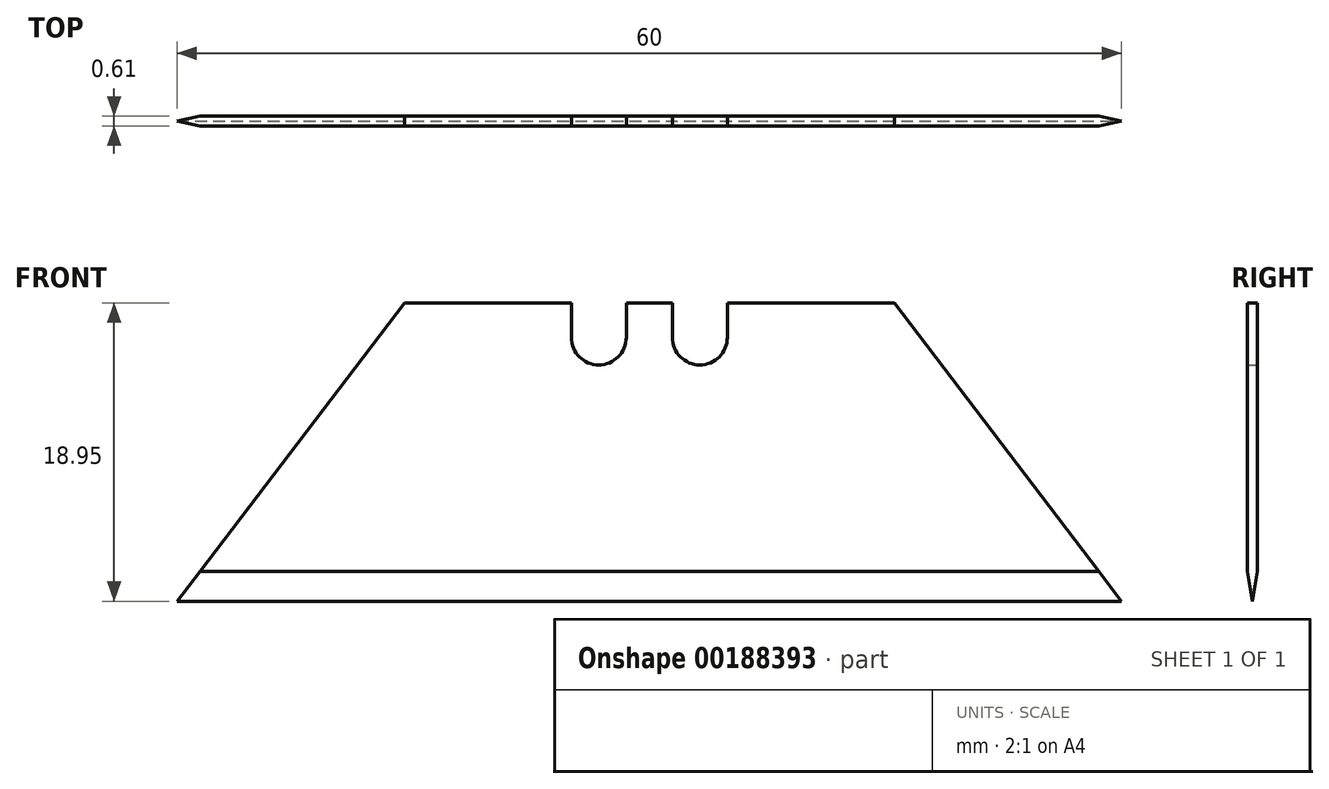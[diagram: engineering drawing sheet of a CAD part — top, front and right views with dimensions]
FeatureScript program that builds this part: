
annotation { "Feature Type Name" : "Feature", "Feature Type Description" : "" }
export const myFeature = defineFeature(function(context is Context, id is Id, definition is map)
    precondition{}
    {
        {
            var Q0;
            Q0=qCreatedBy(makeId("Front.planeOp"),FACE);
            var sketch = newSketch(context, id + "F0", { "sketchPlane" : qUnion([Q0])});
            skLineSegment(sketch, "E0", {"start": v(0, -18.95) * mm, "end": v(-14.44, 0) * mm});
            skLineSegment(sketch, "E1", {"start": v(-14.44, 0) * mm, "end": v(-25.04, 0) * mm});
            skLineSegment(sketch, "E2", {"start": v(-45.56, 0) * mm, "end": v(-60, -18.95) * mm});
            skLineSegment(sketch, "E3", {"start": v(-60, -18.95) * mm, "end": v(0, -18.95) * mm});
            skLineSegment(sketch, "E4", {"start": v(-30, 0) * mm, "end": v(-30, -18.95) * mm, "construction": true});
            skLineSegment(sketch, "E5", {"start": v(-28.54, 0) * mm, "end": v(-28.54, -2.2) * mm});
            skArc(sketch, "E6", {"start": v(-28.54, -2.2) * mm, "mid": v(-26.79, -3.94) * mm, "end": v(-25.04, -2.2) * mm});
            skLineSegment(sketch, "E7", {"start": v(-25.04, -2.2) * mm, "end": v(-25.04, 0) * mm});
            skLineSegment(sketch, "E8.MirrorCS", {"start": v(-31.46, 0) * mm, "end": v(-31.46, -2.2) * mm});
            skArc(sketch, "E9.MirrorCS", {"start": v(-31.46, -2.2) * mm, "mid": v(-33.21, -3.94) * mm, "end": v(-34.96, -2.2) * mm});
            skLineSegment(sketch, "E10.MirrorCS", {"start": v(-34.96, -2.2) * mm, "end": v(-34.96, 0) * mm});
            skLineSegment(sketch, "E11.trimOffspring", {"start": v(-34.96, 0) * mm, "end": v(-45.56, 0) * mm});
            skLineSegment(sketch, "E12.trimOffspring", {"start": v(-28.54, 0) * mm, "end": v(-31.46, 0) * mm});
            skSolve(sketch);
        }
        {
            var Q0;
            Q0 = qSketchRegion(id + "F0", true);
            extrude(context, id + "F1", {"entities" : qUnion([Q0]), "depth" : 0.6 * mm});
        }
        {
            var Q0;
            Q0=qCreatedBy(makeId("Right.planeOp"),FACE);
            var sketch = newSketch(context, id + "F2", { "sketchPlane" : qUnion([Q0])});
            skLineSegment(sketch, "E13", {"start": v(-0.6, -17.04) * mm, "end": v(-0.3, -18.95) * mm});
            skLineSegment(sketch, "E14", {"start": v(-0.3, -18.95) * mm, "end": v(0, -17.04) * mm});
            skLineSegment(sketch, "E15", {"start": v(0, -17.04) * mm, "end": v(-0.6, -17.04) * mm, "construction": true});
            skLineSegment(sketch, "E16.0", {"start": v(-0.6, -18.95) * mm, "end": v(-0.6, -17.04) * mm});
            skLineSegment(sketch, "E17.0", {"start": v(-0.6, -18.95) * mm, "end": v(0, -18.95) * mm});
            skLineSegment(sketch, "E18.0", {"start": v(0, -18.95) * mm, "end": v(0, -17.04) * mm});
            skPoint(sketch, "E19.orphan", {"position": v(-0.6, 0) * mm});
            skPoint(sketch, "E20.orphan", {"position": v(0, 0) * mm});
            skSolve(sketch);
        }
        {
            var Q0;
            {var subQ0=sQuery(id+"F2.wireOp",EDGE,"E14");Q0=makeQuery(id+"F2.imprint","IMPRINT",FACE,{"disambiguationData":[TD([[makeQuery(id+"F2.imprint","IMPRINT",EDGE,{"derivedFrom":subQ0}),-1.0]])]});}
            var Q1;
            {var subQ0=sQuery(id+"F2.wireOp",EDGE,"E13");Q1=makeQuery(id+"F2.imprint","IMPRINT",FACE,{"disambiguationData":[TD([[makeQuery(id+"F2.imprint","IMPRINT",EDGE,{"derivedFrom":subQ0}),-1.0]])]});}
            extrude(context, id + "F3", {"entities" : qUnion([Q0, Q1]), "operationType" : NewBodyOperationType.REMOVE, "endBound" : BoundingType.THROUGH_ALL, "oppositeDirection" : true, "depth" : 25.4 * mm});
        }
    });
